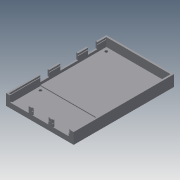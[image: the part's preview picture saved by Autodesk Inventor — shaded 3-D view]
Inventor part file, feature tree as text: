
AUTODESK INVENTOR PART (.ipt)
format: ipt  version: 2015 (Build 190159000, 159)  size: 318,464 bytes
history: native  units: in
note: dims shown in document units (in); Inventor stores cm internally (conversion verified against a paired STEP export)
features: extrude x15, sketch x15, hole x4
ambient origin geometry x8: Origin, YZ Plane, XZ Plane, XY Plane, X Axis, Y Axis, Z Axis, Center Point
bodies: Solid1 (feature_tree)
feature tree (34):
  extrude  "Extrusion1"  Depth=2.4016in
  extrude  "Extrusion2"  Depth=0.0591in
  extrude  "Extrusion3"  Depth=0.0591in
  extrude  "Extrusion4"  Depth=0.3346in TaperAngle=0.0deg
  extrude  "Extrusion5"  Depth=2.2835in
  extrude  "Extrusion6"  Depth=0.3937in
  extrude  "Extrusion7"  Depth=0.5512in
  extrude  "Extrusion8"  Depth=0.1772in
  extrude  "Extrusion9"  Depth=0.6693in
  extrude  "Extrusion10"  Depth=0.0787in TaperAngle=0.0deg
  extrude  "Extrusion11"  Depth=3.4646in
  extrude  "Extrusion12"  Depth=0.3937in
  extrude  "Extrusion13"  Depth=0.315in
  extrude  "Extrusion16"  Depth=0.6299in
  extrude  "Extrusion17"  Depth=0.3346in
  hole  "Hole1"  [1 undecoded]
  hole  "Hole2"  [1 undecoded]
  hole  "Hole3"  [1 undecoded]
  hole  "Hole4"  [1 undecoded]
  sketch  "Sketch1"  dims[d0=3.563in d1=2.4016in]
  sketch  "Sketch2"  dims[d2=0.0591in d3=0.0in d4=0.0591in]
  sketch  "Sketch3"  dims[d5=0.0394in d6=0.0591in]
  sketch  "Sketch4"  dims[d7=0.0591in d8=0.3346in d9=0.0in]
  sketch  "Sketch5"  dims[d10=2.4016in d11=2.2835in]
  sketch  "Sketch6"  dims[d12=0.0591in d13=0.3937in]
  sketch  "Sketch7"  dims[d14=0.1181in d15=0.5512in]
  sketch  "Sketch8"  dims[d16=0.5512in d17=0.1772in]
  sketch  "Sketch9"  dims[d18=0.1378in d19=0.6693in]
  sketch  "Sketch10"  dims[d20=0.0787in d21=0.0787in d22=0.0in]
  sketch  "Sketch11"  dims[d23=3.563in d24=3.4646in]
  sketch  "Sketch12"  dims[d25=0.0591in d26=0.3937in]
  sketch  "Sketch13"  dims[d27=1.122in d28=0.315in]
  sketch  "Sketch16"  dims[d29=0.3937in d30=0.6299in]
  sketch  "Sketch17"  dims[d31=0.3543in d32=0.3346in d33=0.315in d34=0.0787in d35=0.0in d36=0.0394in d37=0.1772in d38=0.0197in d39=0.0394in d40=0.1181in d41=0.0in d42=0.0394in d43=0.1772in d44=0.0197in d45=0.0394in d46=0.1181in d47=0.0in d48=0.0394in d49=0.1772in d50=0.0197in d51=0.0197in d52=0.0394in d53=0.1181in d54=0.0in d55=0.0394in d56=0.1378in d57=0.0394in d58=0.0197in d59=0.1181in d60=0.0in d61=0.0394in d62=3.5018in d63=0.0394in d64=0.0197in d65=0.0in d66=1.122in d67=0.0394in d68=0.0394in d69=0.0197in d70=0.0in d71=0.3937in d72=0.0394in d73=0.0394in d74=0.0197in d75=0.0in d76=0.0394in d77=0.0394in d78=0.0197in d79=0.0in d80=0.0394in d81=0.0394in d82=0.0197in d83=0.0in d92=0.1181in d93=0.0in d94=0.0295in d95=0.0in d96=0.1378in d97=0.1378in d98=0.0984in d99=0.2362in d100=0.1575in d101=0.0787in d102=90.0deg d103=0.315in d104=0.8108in d105=0.1438in d106=0.1378in d107=0.0984in d108=0.2362in d109=0.1575in d110=0.0787in d111=90.0deg d112=0.315in d113=0.8108in d114=0.1378in d115=0.1378in d116=0.0984in d117=0.2362in d118=0.1575in d119=0.0787in d120=90.0deg d121=0.315in d122=0.8108in d123=0.1378in d124=0.1378in d125=0.0984in d126=0.2362in d127=0.1575in d128=0.0787in d129=90.0deg d130=0.315in d131=0.8108in]
note: 4 required parameter values undecoded (feature->parameter linkage not recoverable at this tier; creation-order binding heuristic only, values carry confidence <= 0.55)
